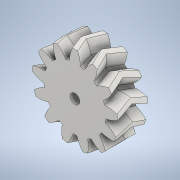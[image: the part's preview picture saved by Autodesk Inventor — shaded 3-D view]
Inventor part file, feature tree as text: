
AUTODESK INVENTOR PART (.ipt)
format: ipt  version: 2020 (Build 240168000, 168)  size: 454,656 bytes
history: native  units: mm (DEFAULTED — no unit token found)
features: plane x3, other x3, sketch x3, extrude x2, mirror x1
ambient origin geometry x8: Origin, YZ Plane, XZ Plane, XY Plane, X Axis, Y Axis, Z Axis, Center Point
bodies: Solid1 (feature_tree)
feature tree (12):
  extrude  "Extrusion1"  Depth=5.0mm TaperAngle=0.0deg
  plane  "Work Plane2"
  plane  "Work Plane8"
  plane  "Work Plane9"
  other  "Spur Gear"
  mirror  "Mirror2"
  extrude  "Extrusion3"  Depth=10.0mm TaperAngle=0.0deg
  sketch  "Sketch1"  dims[d0=28.421877mm d1=5.0mm d2=0.0mm]
  sketch  "Sketch2"  dims[d3=25.0mm d4=10.0mm d5=0.0mm]
  other  "Srf1"
  sketch  "Sketch4"  dims[d16=25.0mm d17=0.0mm d34=2.41661mm d39=0.0mm d41=0.0mm d43=25.0mm d46=25.0mm d47=0.0mm d48=0.0mm d52=3.2mm d53=10.0mm d54=0.0mm]
  other  "Pitch Diameter"
